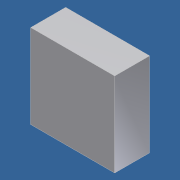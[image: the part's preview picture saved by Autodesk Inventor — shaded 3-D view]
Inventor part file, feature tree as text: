
AUTODESK INVENTOR PART (.ipt)
format: ipt  version: 2012 (Build 160160000, 160)  size: 65,536 bytes
history: native  units: in
note: dims shown in document units (in); Inventor stores cm internally (conversion verified against a paired STEP export)
features: extrude x1, sketch x1
ambient origin geometry x8: Origin, YZ Plane, XZ Plane, XY Plane, X Axis, Y Axis, Z Axis, Center Point
bodies: Solid1 (feature_tree)
feature tree (2):
  extrude  "Extrusion1"  Depth=0.625in TaperAngle=0.0deg
  sketch  "Sketch1"  dims[d0=1.5in d1=0.625in d2=0.0in]
